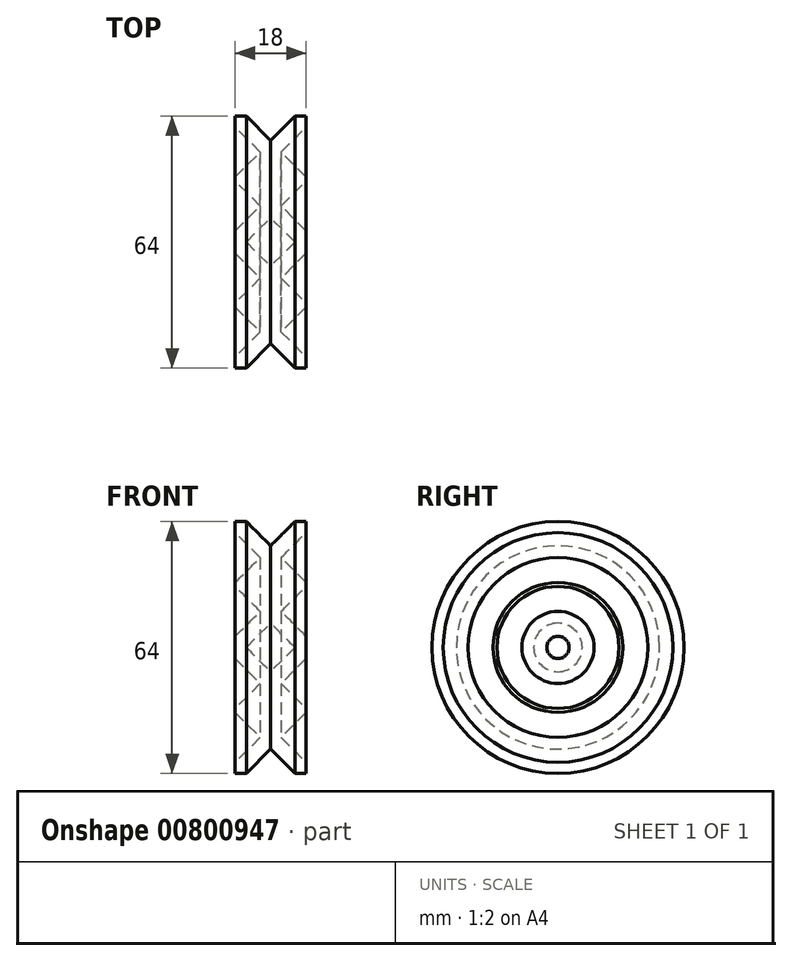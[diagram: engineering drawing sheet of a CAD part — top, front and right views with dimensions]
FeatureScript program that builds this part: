
annotation { "Feature Type Name" : "Feature", "Feature Type Description" : "" }
export const myFeature = defineFeature(function(context is Context, id is Id, definition is map)
    precondition{}
    {
        {
            var Q0;
            Q0=qCreatedBy(makeId("Top.planeOp"),FACE);
            var sketch = newSketch(context, id + "F0", { "sketchPlane" : qUnion([Q0])});
            skLineSegment(sketch, "E0", {"start": v(0, 0) * mm, "end": v(2.83, 0) * mm});
            skLineSegment(sketch, "E1", {"start": v(2.83, 0) * mm, "end": v(9, -6.17) * mm});
            skLineSegment(sketch, "E2", {"start": v(9, -6.17) * mm, "end": v(15.17, 0) * mm});
            skLineSegment(sketch, "E3", {"start": v(15.17, 0) * mm, "end": v(18, 0) * mm});
            skLineSegment(sketch, "E4", {"start": v(18, 0) * mm, "end": v(18, -2.83) * mm});
            skLineSegment(sketch, "E5", {"start": v(18, -2.83) * mm, "end": v(11.66, -9.16) * mm});
            skLineSegment(sketch, "E6", {"start": v(11.66, -22.84) * mm, "end": v(18, -29.17) * mm});
            skLineSegment(sketch, "E7", {"start": v(18, -29.17) * mm, "end": v(18, -32) * mm});
            skLineSegment(sketch, "E8", {"start": v(18, -32) * mm, "end": v(15.17, -32) * mm});
            skLineSegment(sketch, "E9", {"start": v(15.17, -32) * mm, "end": v(9, -25.83) * mm});
            skLineSegment(sketch, "E10", {"start": v(9, -25.83) * mm, "end": v(2.83, -32) * mm});
            skLineSegment(sketch, "E11", {"start": v(2.83, -32) * mm, "end": v(0, -32) * mm});
            skLineSegment(sketch, "E12", {"start": v(0, -32) * mm, "end": v(0, -29.17) * mm});
            skLineSegment(sketch, "E13", {"start": v(0, -29.17) * mm, "end": v(6.34, -22.84) * mm});
            skLineSegment(sketch, "E14", {"start": v(6.34, -22.84) * mm, "end": v(0, -16.5) * mm});
            skLineSegment(sketch, "E15", {"start": v(0, -16.5) * mm, "end": v(0, -15.5) * mm});
            skLineSegment(sketch, "E16", {"start": v(0, -15.5) * mm, "end": v(6.34, -9.16) * mm});
            skLineSegment(sketch, "E17", {"start": v(6.34, -9.16) * mm, "end": v(0, -2.83) * mm});
            skLineSegment(sketch, "E18", {"start": v(0, -2.83) * mm, "end": v(0, 0) * mm});
            skLineSegment(sketch, "E19", {"start": v(11.66, -9.16) * mm, "end": v(18, -15.5) * mm});
            skLineSegment(sketch, "E20", {"start": v(18, -15.5) * mm, "end": v(18, -16.5) * mm});
            skLineSegment(sketch, "E21", {"start": v(18, -16.5) * mm, "end": v(11.66, -22.84) * mm});
            skLineSegment(sketch, "E22", {"start": v(9, -12.16) * mm, "end": v(5.16, -16) * mm});
            skLineSegment(sketch, "E23", {"start": v(5.16, -16) * mm, "end": v(9, -19.84) * mm});
            skLineSegment(sketch, "E24", {"start": v(9, -19.84) * mm, "end": v(12.84, -16) * mm});
            skLineSegment(sketch, "E25", {"start": v(12.84, -16) * mm, "end": v(9, -12.16) * mm});
            skSolve(sketch);
        }
        {
            var Q0;
            Q0=makeQuery(id+"F0.imprint","IMPRINT",FACE,{"disambiguationData":[TD([[makeQuery(id+"F0.imprint","IMPRINT",EDGE,{"derivedFrom":sQuery(id+"F0.wireOp",EDGE,"E0")}),-1.0]])]});
            var Q1;
            Q1=makeQuery(id+"F0.imprint","IMPRINT",FACE,{"disambiguationData":[TD([[makeQuery(id+"F0.imprint","IMPRINT",EDGE,{"derivedFrom":sQuery(id+"F0.wireOp",EDGE,"E22")}),1.0]])]});
            var Q2;
            Q2=sQuery(id+"F0.wireOp",EDGE,"E3");
            revolve(context, id + "F1", {"surfaceOperationType" : NewSurfaceOperationType.NEW, "entities" : qUnion([Q0, Q1]), "axis" : qUnion([Q2]), "revolveType" : RevolveType.FULL});
        }
    });
